# Revit family: Lavatory-TOTO-Contemporary-Lloyd-LPT930.8
name_source: partatom
category: Plumbing Fixtures
revit_build: Autodesk Revit Architecture 2013 (Build: 20130531_2115(x64)
units: mm (PartAtom-declared; Revit-internal decimal feet)

## types (1)
- LPT930.8
    04 CSI = 22 42 16
    95 CSI = 15410
    ADA Compliant = No
    Assembly Code = D2010310
    Basin Depth = 13 1/4"
    Basin Diameter = 0"
    Basin Width = 26 3/8"
    CAD Drawing URL = http://assets.totousa.com
    Certifications = IAPMO(cUPC), State of Massachusetts, City of Los Angeles, and others
    Code Compliance = UPC, IPC, NSPC, NPC Canada, and others
    Cold Water Connection Radius = 1/2"
    Cold Water Connector = Cold Water Connection
    Color Availability = #01 Cotton, #03 Bone, #11 Colonial White, #12 Sedona Beige, #51 Ebony
    Default Elevation = 48"
    Depth = 19 5/8"
    Description = Lloyd® Metal Console Lavatory
    Diameter = 0"
    Finish = Vitreous China - TOTO - 01 Cotton
    Height = 34 1/4"
    Hot Water Connection Radius = 1/2"
    Hot Water Connector = Hot Water Connection
    Industry Standards = Meets and exceeds ASME A112.19.2/CSA B45.1
    Manufacturer = TOTO USA, Inc.
    Manufacturer Fax = (770) 282-0002
    Material = Fired clay china
    Model = LPT930.8
    Sanitary Connector = Sanitary Connection
    SanoGloss Available = No
    Series = Lloyd
    Shipping Weight = 53.00 lb
    Spec Sheet URL = http://assets.totousa.com
    Style = Contemporary
    Subcategory = Lavatories
    Toto BIM Number = BM-00347
    URL = http://www.totousa.com
    Warranty = One Year Limited Warranty
    Warranty URL = http://www.totousa.com
    Waste Connection Radius = 5/8"
    Width = 28 3/4"

## geometry (parser evidence)
native form markers: Blend x10, Sweep x3
no freeform markers — native parametric forms only
